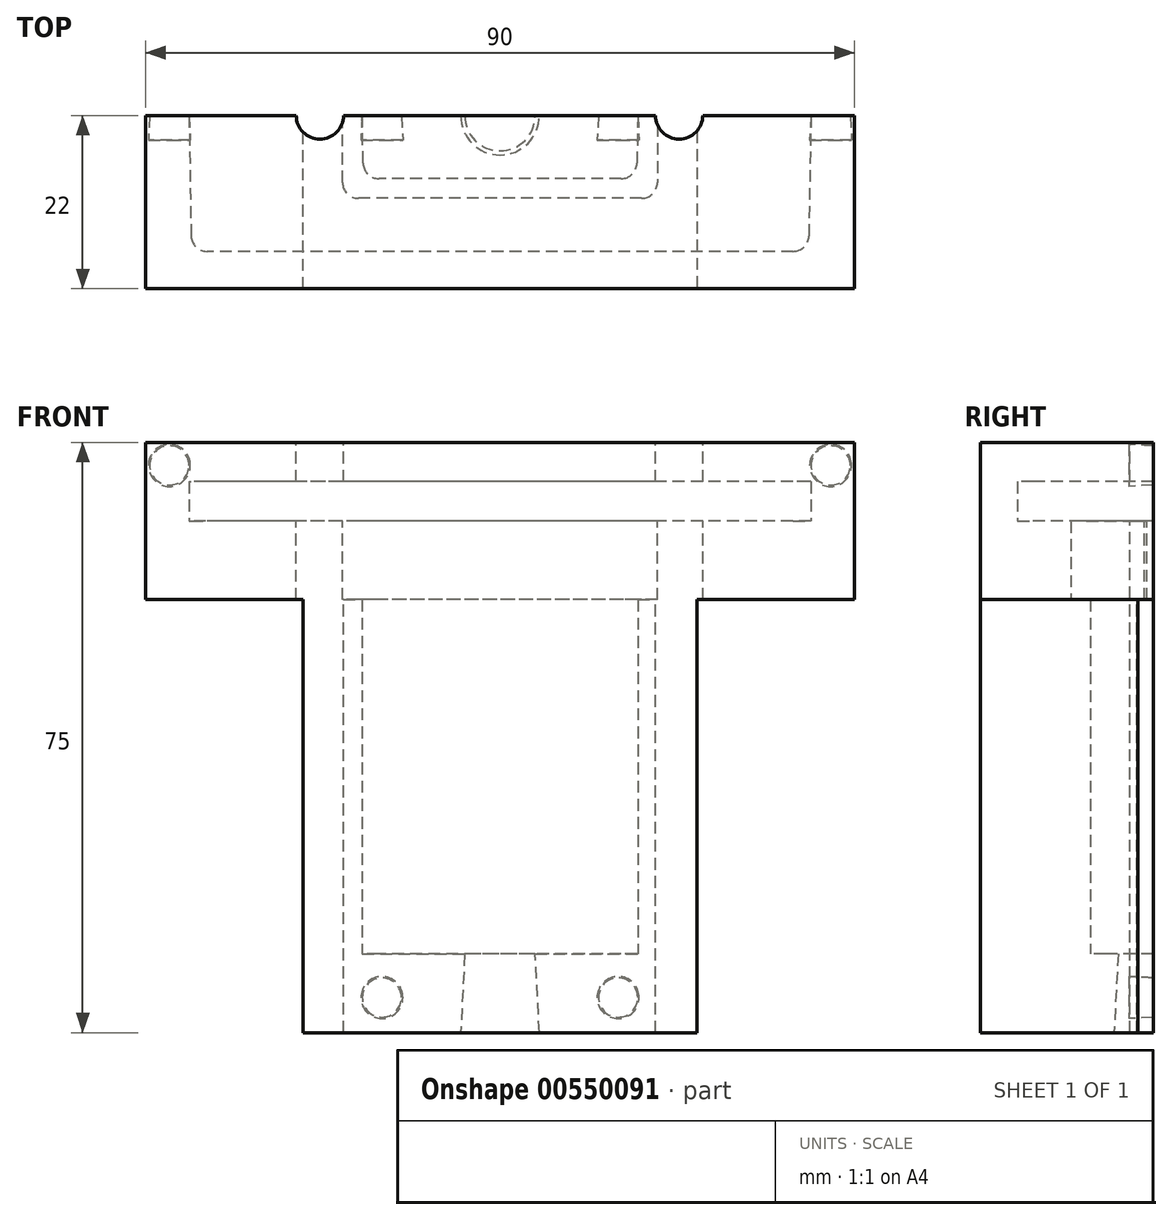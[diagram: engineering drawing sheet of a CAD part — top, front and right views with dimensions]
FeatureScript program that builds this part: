
annotation { "Feature Type Name" : "Feature", "Feature Type Description" : "" }
export const myFeature = defineFeature(function(context is Context, id is Id, definition is map)
    precondition{}
    {
        {
            var Q0;
            Q0=qCreatedBy(makeId("Top.planeOp"),FACE);
            var sketch = newSketch(context, id + "F0", { "sketchPlane" : qUnion([Q0])});
            skLineSegment(sketch, "E0.bottom", {"start": v(45, -44.53) * mm, "end": v(-45, -44.53) * mm});
            skLineSegment(sketch, "E0.top", {"start": v(45, -66.53) * mm, "end": v(-45, -66.53) * mm});
            skLineSegment(sketch, "E0.left", {"start": v(45, -44.53) * mm, "end": v(45, -66.53) * mm});
            skLineSegment(sketch, "E0.right", {"start": v(-45, -44.53) * mm, "end": v(-45, -66.53) * mm});
            skPoint(sketch, "E0.middle", {"position": v(0, -55.53) * mm});
            skSolve(sketch);
        }
        {
            var Q0;
            Q0=qSketchRegion(id+"F0",true);
            extrude(context, id + "F1", {"entities" : qUnion([Q0]), "depth" : 10 * mm, "offsetDistance" : 25 * mm});
        }
        {
            var Q0;
            Q0=makeQuery(id+"F1.opExtrude","CAP_FACE",FACE,{"disambiguationData":[OSD([sQuery(id+"F0.wireOp",EDGE,"E0.bottom"),sQuery(id+"F0.wireOp",EDGE,"E0.top"),sQuery(id+"F0.wireOp",EDGE,"E0.left"),sQuery(id+"F0.wireOp",EDGE,"E0.right")])],"isStart":true});
            var sketch = newSketch(context, id + "F2", { "sketchPlane" : qUnion([Q0])});
            skLineSegment(sketch, "E1", {"start": v(0, 44.53) * mm, "end": v(39.5, 44.53) * mm});
            skLineSegment(sketch, "E2", {"start": v(39.5, 44.53) * mm, "end": v(39.5, 61.78) * mm});
            skLineSegment(sketch, "E3", {"start": v(39.5, 61.78) * mm, "end": v(-39.5, 61.78) * mm});
            skLineSegment(sketch, "E4", {"start": v(-39.5, 61.78) * mm, "end": v(-39.5, 44.53) * mm});
            skLineSegment(sketch, "E5", {"start": v(-39.5, 44.53) * mm, "end": v(0, 44.53) * mm});
            skLineSegment(sketch, "E6", {"start": v(-39.5, 44.53) * mm, "end": v(-39.2, 61.78) * mm});
            skLineSegment(sketch, "E7", {"start": v(39.5, 44.53) * mm, "end": v(39.2, 61.78) * mm});
            skSolve(sketch);
        }
        {
            var Q0;
            Q0=makeQuery(id+"F2.imprint","IMPRINT",FACE,{"disambiguationData":[TD([[makeQuery(id+"F2.imprint","IMPRINT",EDGE,{"derivedFrom":sQuery(id+"F2.wireOp",EDGE,"E1")}),-1.0]])]});
            extrude(context, id + "F3", {"entities" : qUnion([Q0]), "operationType" : NewBodyOperationType.REMOVE, "oppositeDirection" : true, "depth" : 5 * mm, "offsetDistance" : 25 * mm});
        }
        {
            var Q0;
            Q0=makeQuery(id+"F3.boolean.opBoolean","COPY",EDGE,{"derivedFrom":makeQuery(id+"F3.opExtrude","SWEPT_EDGE",EDGE,{"disambiguationData":[OSD([sQuery(id+"F2.wireOp",EDGE,"E3"),sQuery(id+"F2.wireOp",EDGE,"E6")])]})});
            var Q1;
            Q1=makeQuery(id+"F3.boolean.opBoolean","COPY",EDGE,{"derivedFrom":makeQuery(id+"F3.opExtrude","SWEPT_EDGE",EDGE,{"disambiguationData":[OSD([sQuery(id+"F2.wireOp",EDGE,"E3"),sQuery(id+"F2.wireOp",EDGE,"E7")])]})});
            fillet(context, id + "F4", {"entities" : qUnion([Q0, Q1]), "radius" : 2 * mm, "tangentPropagation" : true, "allowEdgeOverflow" : false});
        }
        {
            var Q0;
            Q0=makeQuery(id+"F1.opExtrude","CAP_FACE",FACE,{"disambiguationData":[OSD([sQuery(id+"F0.wireOp",EDGE,"E0.bottom"),sQuery(id+"F0.wireOp",EDGE,"E0.top"),sQuery(id+"F0.wireOp",EDGE,"E0.left"),sQuery(id+"F0.wireOp",EDGE,"E0.right")])],"isStart":true});
            var sketch = newSketch(context, id + "F5", { "sketchPlane" : qUnion([Q0])});
            skLineSegment(sketch, "E8", {"start": v(-45, 44.53) * mm, "end": v(45, 44.53) * mm});
            skLineSegment(sketch, "E9", {"start": v(45, 44.53) * mm, "end": v(45, 66.53) * mm});
            skLineSegment(sketch, "E10", {"start": v(45, 66.53) * mm, "end": v(-45, 66.53) * mm});
            skLineSegment(sketch, "E11", {"start": v(-45, 66.53) * mm, "end": v(-45, 44.53) * mm});
            skSolve(sketch);
        }
        {
            var Q0;
            Q0=qSketchRegion(id+"F5",true);
            extrude(context, id + "F6", {"entities" : qUnion([Q0]), "operationType" : NewBodyOperationType.ADD, "depth" : 10 * mm, "offsetDistance" : 25 * mm});
        }
        {
            var Q0;
            Q0=makeQuery(id+"F6.opExtrude","CAP_FACE",FACE,{"disambiguationData":[OSD([sQuery(id+"F5.wireOp",EDGE,"E8"),sQuery(id+"F5.wireOp",EDGE,"E9"),sQuery(id+"F5.wireOp",EDGE,"E10"),sQuery(id+"F5.wireOp",EDGE,"E11")])],"isStart":false});
            var sketch = newSketch(context, id + "F7", { "sketchPlane" : qUnion([Q0])});
            skLineSegment(sketch, "E12", {"start": v(0, 44.53) * mm, "end": v(20, 44.53) * mm});
            skLineSegment(sketch, "E13", {"start": v(20, 44.53) * mm, "end": v(20, 55.03) * mm});
            skLineSegment(sketch, "E14", {"start": v(20, 55.03) * mm, "end": v(-20, 55.03) * mm});
            skLineSegment(sketch, "E15", {"start": v(-20, 55.03) * mm, "end": v(-20, 44.53) * mm});
            skLineSegment(sketch, "E16", {"start": v(-20, 44.53) * mm, "end": v(0, 44.53) * mm});
            skLineSegment(sketch, "E17", {"start": v(-20, 44.53) * mm, "end": v(-19.82, 55.03) * mm});
            skLineSegment(sketch, "E18", {"start": v(20, 44.53) * mm, "end": v(19.82, 55.03) * mm});
            skSolve(sketch);
        }
        {
            var Q0;
            Q0=qSketchRegion(id+"F7",true);
            var Q1;
            Q1=makeQuery(id+"F7.imprint","IMPRINT",FACE,{"disambiguationData":[TD([[makeQuery(id+"F7.imprint","IMPRINT",EDGE,{"derivedFrom":sQuery(id+"F7.wireOp",EDGE,"E12")}),-1.0]])]});
            extrude(context, id + "F8", {"entities" : qUnion([Q0, Q1]), "operationType" : NewBodyOperationType.REMOVE, "oppositeDirection" : true, "depth" : 10 * mm, "offsetDistance" : 25 * mm});
        }
        {
            var Q0;
            Q0=makeQuery(id+"F8.boolean.opBoolean","COPY",EDGE,{"derivedFrom":makeQuery(id+"F8.opExtrude","SWEPT_EDGE",EDGE,{"disambiguationData":[OSD([sQuery(id+"F7.wireOp",EDGE,"E14"),sQuery(id+"F7.wireOp",EDGE,"E15")])]})});
            var Q1;
            Q1=makeQuery(id+"F8.boolean.opBoolean","COPY",EDGE,{"derivedFrom":makeQuery(id+"F8.opExtrude","SWEPT_EDGE",EDGE,{"disambiguationData":[OSD([sQuery(id+"F7.wireOp",EDGE,"E13"),sQuery(id+"F7.wireOp",EDGE,"E14")])]})});
            fillet(context, id + "F9", {"entities" : qUnion([Q0, Q1]), "radius" : 2 * mm, "tangentPropagation" : true, "allowEdgeOverflow" : false});
        }
        {
            var Q0;
            Q0=makeQuery(id+"F6.opExtrude","CAP_FACE",FACE,{"disambiguationData":[OSD([sQuery(id+"F5.wireOp",EDGE,"E8"),sQuery(id+"F5.wireOp",EDGE,"E9"),sQuery(id+"F5.wireOp",EDGE,"E10"),sQuery(id+"F5.wireOp",EDGE,"E11")])],"isStart":false});
            var sketch = newSketch(context, id + "F10", { "sketchPlane" : qUnion([Q0])});
            skLineSegment(sketch, "E19", {"start": v(0, 44.53) * mm, "end": v(25, 44.53) * mm});
            skLineSegment(sketch, "E20", {"start": v(25, 44.53) * mm, "end": v(25, 66.53) * mm});
            skLineSegment(sketch, "E21", {"start": v(25, 66.53) * mm, "end": v(-25, 66.53) * mm});
            skLineSegment(sketch, "E22", {"start": v(-25, 66.53) * mm, "end": v(-25, 44.53) * mm});
            skLineSegment(sketch, "E23", {"start": v(-25, 44.53) * mm, "end": v(0, 44.53) * mm});
            skSolve(sketch);
        }
        {
            var Q0;
            Q0=qSketchRegion(id+"F10",true);
            extrude(context, id + "F11", {"entities" : qUnion([Q0]), "operationType" : NewBodyOperationType.ADD, "depth" : 45 * mm, "offsetDistance" : 25 * mm});
        }
        {
            var Q0;
            Q0=makeQuery(id+"F11.opExtrude","CAP_FACE",FACE,{"disambiguationData":[OSD([sQuery(id+"F10.wireOp",EDGE,"E19"),sQuery(id+"F10.wireOp",EDGE,"E20"),sQuery(id+"F10.wireOp",EDGE,"E21"),sQuery(id+"F10.wireOp",EDGE,"E22"),sQuery(id+"F10.wireOp",EDGE,"E23")])],"isStart":false});
            var sketch = newSketch(context, id + "F12", { "sketchPlane" : qUnion([Q0])});
            skLineSegment(sketch, "E24", {"start": v(0, 44.53) * mm, "end": v(17.5, 44.53) * mm});
            skLineSegment(sketch, "E25", {"start": v(17.5, 44.53) * mm, "end": v(17.5, 52.53) * mm});
            skLineSegment(sketch, "E26", {"start": v(17.5, 52.53) * mm, "end": v(-17.5, 52.53) * mm});
            skLineSegment(sketch, "E27", {"start": v(-17.5, 52.53) * mm, "end": v(-17.5, 44.53) * mm});
            skLineSegment(sketch, "E28", {"start": v(-17.5, 44.53) * mm, "end": v(0, 44.53) * mm});
            skLineSegment(sketch, "E29", {"start": v(-17.36, 52.53) * mm, "end": v(-17.5, 44.53) * mm});
            skLineSegment(sketch, "E30", {"start": v(17.5, 44.53) * mm, "end": v(17.36, 52.53) * mm});
            skSolve(sketch);
        }
        {
            var Q0;
            Q0=makeQuery(id+"F12.imprint","IMPRINT",FACE,{"disambiguationData":[TD([[makeQuery(id+"F12.imprint","IMPRINT",EDGE,{"derivedFrom":sQuery(id+"F12.wireOp",EDGE,"E24")}),1.0]])]});
            extrude(context, id + "F13", {"entities" : qUnion([Q0]), "operationType" : NewBodyOperationType.REMOVE, "oppositeDirection" : true, "depth" : 45 * mm, "offsetDistance" : 25 * mm});
        }
        {
            var Q0;
            Q0=makeQuery(id+"F13.boolean.opBoolean","COPY",EDGE,{"derivedFrom":makeQuery(id+"F13.opExtrude","SWEPT_EDGE",EDGE,{"disambiguationData":[OSD([sQuery(id+"F12.wireOp",EDGE,"E26"),sQuery(id+"F12.wireOp",EDGE,"E29")])]})});
            var Q1;
            Q1=makeQuery(id+"F13.boolean.opBoolean","COPY",EDGE,{"derivedFrom":makeQuery(id+"F13.opExtrude","SWEPT_EDGE",EDGE,{"disambiguationData":[OSD([sQuery(id+"F12.wireOp",EDGE,"E26"),sQuery(id+"F12.wireOp",EDGE,"E30")])]})});
            fillet(context, id + "F14", {"entities" : qUnion([Q0, Q1]), "radius" : 2 * mm, "tangentPropagation" : true, "allowEdgeOverflow" : false});
        }
        {
            var Q0;
            Q0=makeQuery(id+"F11.opExtrude","CAP_FACE",FACE,{"disambiguationData":[OSD([sQuery(id+"F10.wireOp",EDGE,"E19"),sQuery(id+"F10.wireOp",EDGE,"E20"),sQuery(id+"F10.wireOp",EDGE,"E21"),sQuery(id+"F10.wireOp",EDGE,"E22"),sQuery(id+"F10.wireOp",EDGE,"E23")])],"isStart":false});
            var sketch = newSketch(context, id + "F15", { "sketchPlane" : qUnion([Q0])});
            skLineSegment(sketch, "E31.bottom", {"start": v(-25, 66.53) * mm, "end": v(25, 66.53) * mm});
            skLineSegment(sketch, "E31.top", {"start": v(-25, 44.53) * mm, "end": v(25, 44.53) * mm});
            skLineSegment(sketch, "E31.left", {"start": v(-25, 66.53) * mm, "end": v(-25, 44.53) * mm});
            skLineSegment(sketch, "E31.right", {"start": v(25, 66.53) * mm, "end": v(25, 44.53) * mm});
            skSolve(sketch);
        }
        {
            var Q0;
            Q0=qSketchRegion(id+"F15",true);
            extrude(context, id + "F16", {"entities" : qUnion([Q0]), "operationType" : NewBodyOperationType.ADD, "depth" : 10 * mm, "offsetDistance" : 25 * mm});
        }
        {
            var Q0;
            Q0=makeQuery(id+"F16.opExtrude","CAP_FACE",FACE,{"disambiguationData":[OSD([sQuery(id+"F15.wireOp",EDGE,"E31.bottom"),sQuery(id+"F15.wireOp",EDGE,"E31.top"),sQuery(id+"F15.wireOp",EDGE,"E31.left"),sQuery(id+"F15.wireOp",EDGE,"E31.right")])],"isStart":false});
            var sketch = newSketch(context, id + "F17", { "sketchPlane" : qUnion([Q0])});
            skCircle(sketch, "E32", {"center": v(0, 44.53) * mm, "radius": 5 * mm});
            skSolve(sketch);
        }
        {
            var Q0;
            Q0=qSketchRegion(id+"F17",true);
            extrude(context, id + "F18", {"entities" : qUnion([Q0]), "operationType" : NewBodyOperationType.REMOVE, "oppositeDirection" : true, "depth" : 25 * mm, "offsetDistance" : 25 * mm, "hasDraft" : true, "draftAngle" : 3 * degree, "draftPullDirection" : true});
        }
        {
            var Q0;
            Q0=makeQuery(id+"F1.opExtrude","CAP_FACE",FACE,{"disambiguationData":[OSD([sQuery(id+"F0.wireOp",EDGE,"E0.bottom"),sQuery(id+"F0.wireOp",EDGE,"E0.top"),sQuery(id+"F0.wireOp",EDGE,"E0.left"),sQuery(id+"F0.wireOp",EDGE,"E0.right")])],"isStart":false});
            var sketch = newSketch(context, id + "F19", { "sketchPlane" : qUnion([Q0])});
            skLineSegment(sketch, "E33", {"start": v(0, -44.53) * mm, "end": v(22.8, -44.53) * mm});
            skLineSegment(sketch, "E34", {"start": v(0, -44.53) * mm, "end": v(-22.8, -44.53) * mm});
            skSolve(sketch);
        }
        {
            var Q0;
            {var subQ2=sQuery(id+"F19.wireOp",EDGE,"E33");Q0=makeQuery(id+"F19.imprint","IMPRINT",FACE,{"disambiguationData":[TD([[makeQuery(id+"F19.imprint","IMPRINT",EDGE,{"derivedFrom":subQ2}),1.0]])]});}
            var sketch = newSketch(context, id + "F20", { "sketchPlane" : qUnion([Q0])});
            skCircle(sketch, "E35", {"center": v(22.75, -44.52) * mm, "radius": 3 * mm});
            skCircle(sketch, "E36", {"center": v(-22.89, -44.52) * mm, "radius": 3 * mm});
            skSolve(sketch);
        }
        {
            var Q0;
            Q0=qSketchRegion(id+"F20",true);
            extrude(context, id + "F21", {"entities" : qUnion([Q0]), "operationType" : NewBodyOperationType.REMOVE, "oppositeDirection" : true, "depth" : 90 * mm, "offsetDistance" : 25 * mm});
        }
        {
            var Q0;
            {var subQ0=sQuery(id+"F15.wireOp",EDGE,"E31.right");var subQ1=sQuery(id+"F15.wireOp",EDGE,"E31.left");var subQ2=sQuery(id+"F15.wireOp",EDGE,"E31.top");var subQ3=sQuery(id+"F15.wireOp",EDGE,"E31.bottom");var subQ4=sQuery(id+"F10.wireOp",EDGE,"E23");var subQ5=sQuery(id+"F10.wireOp",EDGE,"E19");Q0=makeQuery(id+"F21.boolean.opBoolean","SPLIT",FACE,{"disambiguationData":[TD([makeQuery(id+"F11.opExtrude","CAP_FACE",FACE,{"disambiguationData":[OSD([subQ5,sQuery(id+"F10.wireOp",EDGE,"E20"),sQuery(id+"F10.wireOp",EDGE,"E21"),sQuery(id+"F10.wireOp",EDGE,"E22"),subQ4])],"isStart":true}),makeQuery(id+"F13.boolean.opBoolean","COPY",FACE,{"derivedFrom":makeQuery(id+"F13.opExtrude","SWEPT_FACE",FACE,{"disambiguationData":[OSD([sQuery(id+"F12.wireOp",EDGE,"E30")])]})}),makeQuery(id+"F16.opExtrude","CAP_FACE",FACE,{"disambiguationData":[OSD([subQ3,subQ2,subQ1,subQ0])],"isStart":true}),makeQuery(id+"F16.opExtrude","CAP_FACE",FACE,{"disambiguationData":[OSD([subQ3,subQ2,subQ1,subQ0])],"isStart":false}),makeQuery(id+"F18.boolean.opBoolean","COPY",FACE,{"derivedFrom":makeQuery(id+"F18.opExtrude","SWEPT_FACE",FACE,{"disambiguationData":[OSD([sQuery(id+"F17.wireOp",EDGE,"E32")])]})}),makeQuery(id+"F21.opExtrude","SWEPT_FACE",FACE,{"disambiguationData":[OSD([sQuery(id+"F20.wireOp",EDGE,"E35")])]})])],"derivedFrom":makeQuery(id+"F16.boolean.opBoolean","MERGE",FACE,{"derivedFrom":[makeQuery(id+"F11.boolean.opBoolean","MERGE",FACE,{"derivedFrom":[makeQuery(id+"F6.boolean.opBoolean","MERGE",FACE,{"derivedFrom":[makeQuery(id+"F1.opExtrude","SWEPT_FACE",FACE,{"disambiguationData":[OSD([sQuery(id+"F0.wireOp",EDGE,"E0.bottom")])]}),makeQuery(id+"F6.opExtrude","SWEPT_FACE",FACE,{"disambiguationData":[OSD([sQuery(id+"F5.wireOp",EDGE,"E8")])]})]}),makeQuery(id+"F11.opExtrude","SWEPT_FACE",FACE,{"disambiguationData":[OSD([subQ5,subQ4])]})]}),makeQuery(id+"F16.opExtrude","SWEPT_FACE",FACE,{"disambiguationData":[OSD([subQ2])]})]})});}
            var sketch = newSketch(context, id + "F22", { "sketchPlane" : qUnion([Q0])});
            skCircle(sketch, "E37", {"center": v(-15, -60.54) * mm, "radius": 2.5 * mm});
            skCircle(sketch, "E38.MirrorC", {"center": v(15, -60.54) * mm, "radius": 2.5 * mm});
            skSolve(sketch);
        }
        {
            var Q0;
            Q0=qSketchRegion(id+"F22",true);
            extrude(context, id + "F23", {"entities" : qUnion([Q0]), "operationType" : NewBodyOperationType.REMOVE, "oppositeDirection" : true, "depth" : 3.1 * mm, "offsetDistance" : 25 * mm, "hasDraft" : true, "draftAngle" : 3 * degree});
        }
        {
            var Q0;
            {var subQ0=sQuery(id+"F2.wireOp",EDGE,"E7");var subQ1=sQuery(id+"F0.wireOp",EDGE,"E0.left");var subQ2=sQuery(id+"F0.wireOp",EDGE,"E0.bottom");var subQ3=sQuery(id+"F5.wireOp",EDGE,"E9");var subQ4=sQuery(id+"F5.wireOp",EDGE,"E11");var subQ5=sQuery(id+"F5.wireOp",EDGE,"E10");var subQ6=sQuery(id+"F5.wireOp",EDGE,"E8");Q0=makeQuery(id+"F21.boolean.opBoolean","SPLIT",FACE,{"disambiguationData":[TD([makeQuery(id+"F1.opExtrude","CAP_FACE",FACE,{"disambiguationData":[OSD([subQ2,sQuery(id+"F0.wireOp",EDGE,"E0.top"),subQ1,sQuery(id+"F0.wireOp",EDGE,"E0.right")])],"isStart":false}),makeQuery(id+"F1.opExtrude","SWEPT_FACE",FACE,{"disambiguationData":[OSD([subQ1])]}),makeQuery(id+"F3.boolean.opBoolean","COPY",FACE,{"derivedFrom":makeQuery(id+"F3.opExtrude","CAP_FACE",FACE,{"disambiguationData":[OSD([sQuery(id+"F2.wireOp",EDGE,"E1"),sQuery(id+"F2.wireOp",EDGE,"E3"),sQuery(id+"F2.wireOp",EDGE,"E5"),sQuery(id+"F2.wireOp",EDGE,"E6"),subQ0])],"isStart":false})}),makeQuery(id+"F3.boolean.opBoolean","COPY",FACE,{"derivedFrom":makeQuery(id+"F3.opExtrude","SWEPT_FACE",FACE,{"disambiguationData":[OSD([subQ0])]})}),makeQuery(id+"F6.opExtrude","CAP_FACE",FACE,{"disambiguationData":[OSD([subQ6,subQ3,subQ5,subQ4])],"isStart":true}),makeQuery(id+"F6.opExtrude","CAP_FACE",FACE,{"disambiguationData":[OSD([subQ6,subQ3,subQ5,subQ4])],"isStart":false}),makeQuery(id+"F6.opExtrude","SWEPT_FACE",FACE,{"disambiguationData":[OSD([subQ3])]}),makeQuery(id+"F21.opExtrude","SWEPT_FACE",FACE,{"disambiguationData":[OSD([sQuery(id+"F20.wireOp",EDGE,"E35")])]})])],"derivedFrom":makeQuery(id+"F16.boolean.opBoolean","MERGE",FACE,{"derivedFrom":[makeQuery(id+"F11.boolean.opBoolean","MERGE",FACE,{"derivedFrom":[makeQuery(id+"F6.boolean.opBoolean","MERGE",FACE,{"derivedFrom":[makeQuery(id+"F1.opExtrude","SWEPT_FACE",FACE,{"disambiguationData":[OSD([subQ2])]}),makeQuery(id+"F6.opExtrude","SWEPT_FACE",FACE,{"disambiguationData":[OSD([subQ6])]})]}),makeQuery(id+"F11.opExtrude","SWEPT_FACE",FACE,{"disambiguationData":[OSD([sQuery(id+"F10.wireOp",EDGE,"E19"),sQuery(id+"F10.wireOp",EDGE,"E23")])]})]}),makeQuery(id+"F16.opExtrude","SWEPT_FACE",FACE,{"disambiguationData":[OSD([sQuery(id+"F15.wireOp",EDGE,"E31.top")])]})]})});}
            var sketch = newSketch(context, id + "F24", { "sketchPlane" : qUnion([Q0])});
            skCircle(sketch, "E39", {"center": v(-42, 7.06) * mm, "radius": 2.5 * mm});
            skCircle(sketch, "E40.MirrorC", {"center": v(42, 7.06) * mm, "radius": 2.5 * mm});
            skSolve(sketch);
        }
        {
            var Q0;
            Q0=qSketchRegion(id+"F24",true);
            extrude(context, id + "F25", {"entities" : qUnion([Q0]), "operationType" : NewBodyOperationType.REMOVE, "oppositeDirection" : true, "depth" : 3.1 * mm, "offsetDistance" : 25 * mm, "hasDraft" : true, "draftAngle" : 3 * degree});
        }
    });
